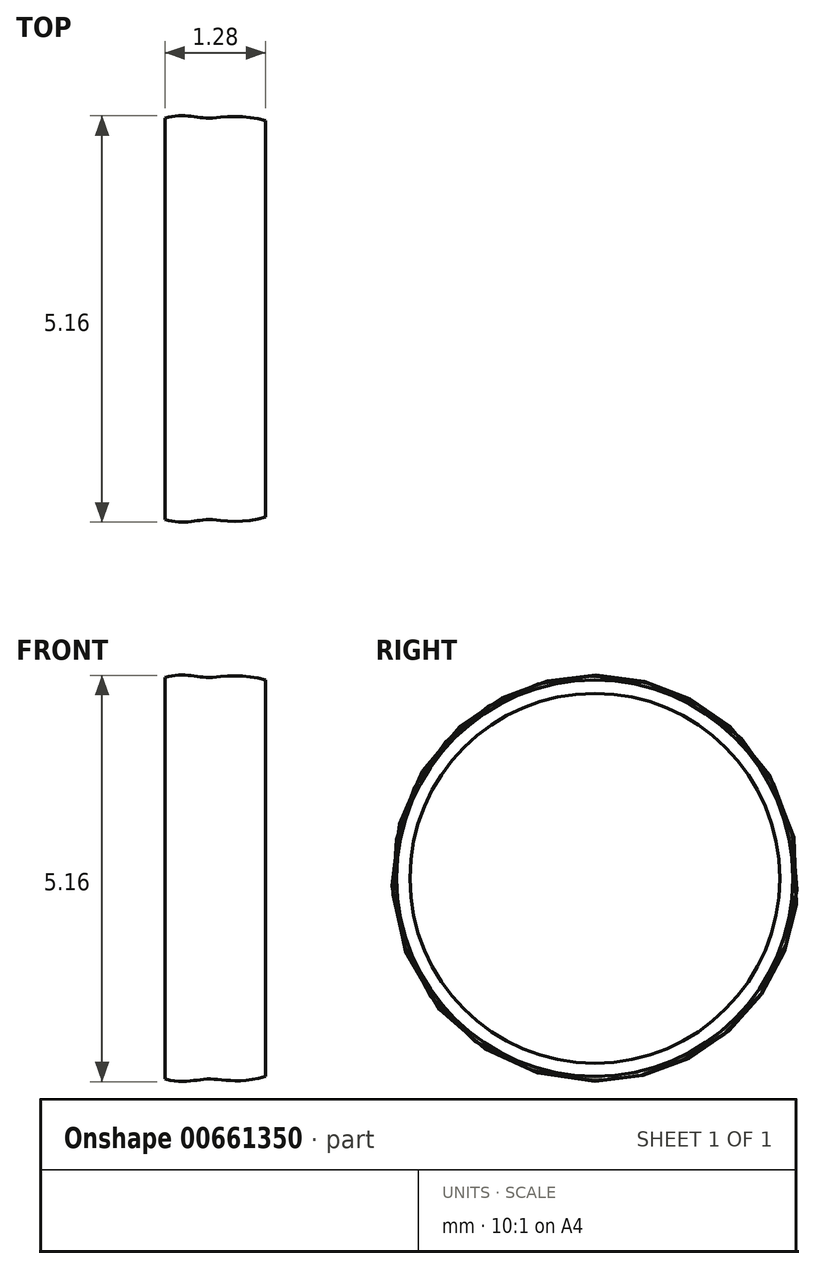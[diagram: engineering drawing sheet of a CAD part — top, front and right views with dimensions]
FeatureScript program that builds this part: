
annotation { "Feature Type Name" : "Feature", "Feature Type Description" : "" }
export const myFeature = defineFeature(function(context is Context, id is Id, definition is map)
    precondition{}
    {
        {
            var Q0;
            Q0=qCreatedBy(makeId("Front.planeOp"),FACE);
            var sketch = newSketch(context, id + "F0", { "sketchPlane" : qUnion([Q0])});
            skFitSpline(sketch, "E0", {"points": [v(2.13, 1.23) * mm, v(2.63, 1.23) * mm, v(3.4, 1.27) * mm], "startDerivative": vector(1.5, -0.46) * mm, "endDerivative": vector(2.15, 0.57) * mm});
            skLineSegment(sketch, "E1", {"start": v(2.13, 1.23) * mm, "end": v(2.63, 1.23) * mm, "construction": true});
            skLineSegment(sketch, "E2", {"start": v(2.13, 3.78) * mm, "end": v(4.4, 3.78) * mm, "construction": true});
            skLineSegment(sketch, "E3", {"start": v(2.13, 1.23) * mm, "end": v(2.13, 1.43) * mm});
            skLineSegment(sketch, "E4", {"start": v(2.13, 3.78) * mm, "end": v(2.13, 1.23) * mm, "construction": true});
            skLineSegment(sketch, "E5", {"start": v(2.86, 2.33) * mm, "end": v(2.86, 2.76) * mm});
            skLineSegment(sketch, "E6", {"start": v(3.87, 2.28) * mm, "end": v(3.87, 2.72) * mm});
            skSolve(sketch);
        }
        {
            var Q0;
            Q0=sQuery(id+"F0.wireOp",EDGE,"E0");
            var Q1;
            Q1=sQuery(id+"F0.wireOp",EDGE,"E3");
            var Q2;
            Q2=sQuery(id+"F0.wireOp",EDGE,"E2");
            revolve(context, id + "F1", {"bodyType" : ToolBodyType.SURFACE, "surfaceEntities" : qUnion([Q0, Q1]), "axis" : qUnion([Q2]), "revolveType" : RevolveType.FULL});
        }
    });
